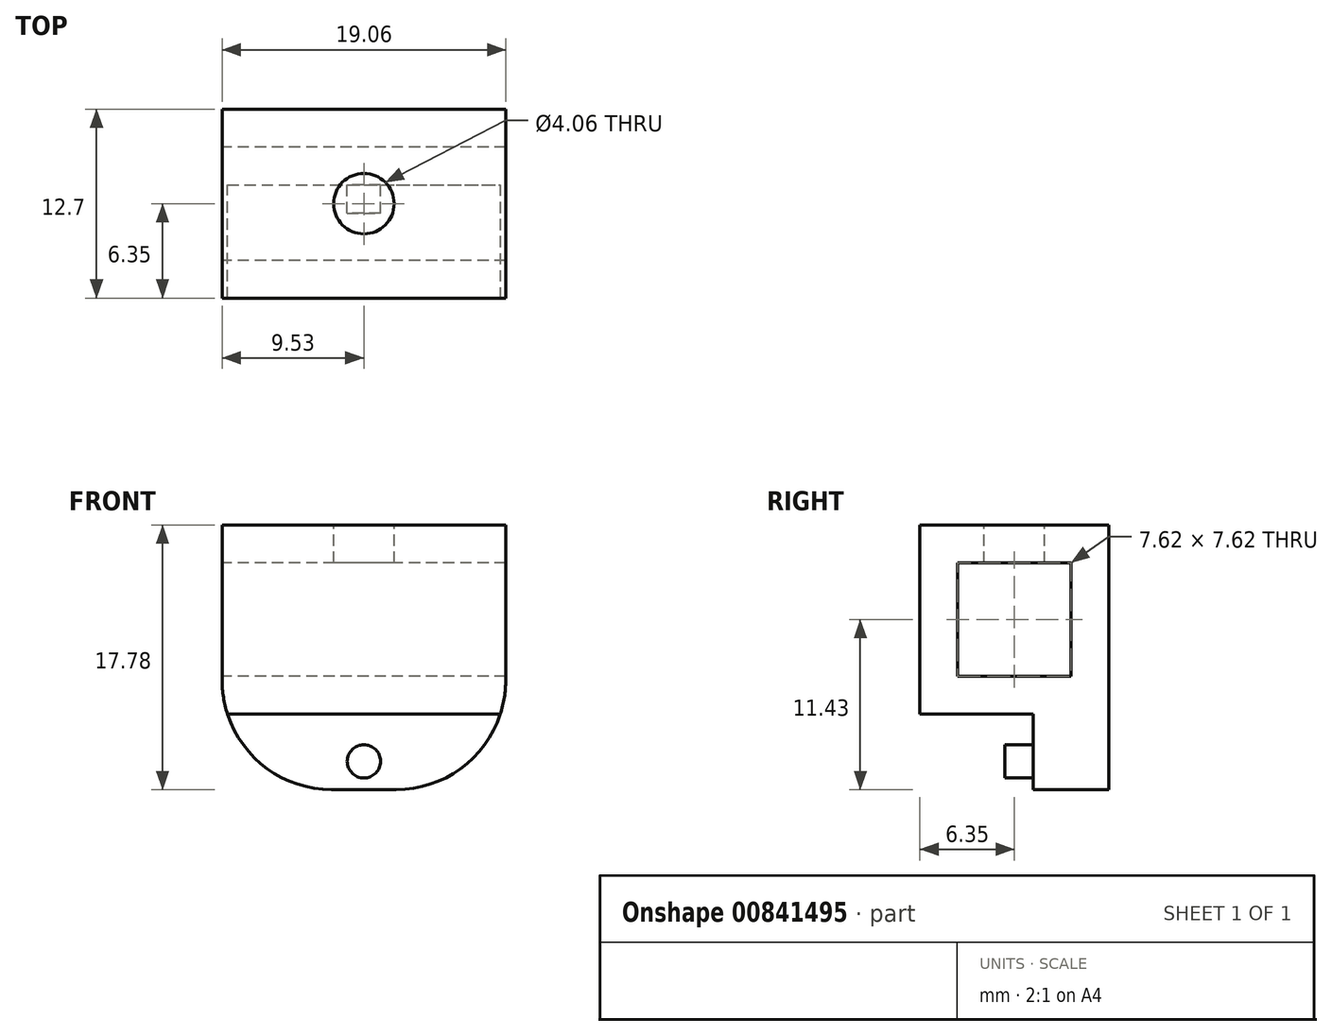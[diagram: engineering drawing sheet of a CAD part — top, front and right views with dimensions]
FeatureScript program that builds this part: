
annotation { "Feature Type Name" : "Feature", "Feature Type Description" : "" }
export const myFeature = defineFeature(function(context is Context, id is Id, definition is map)
    precondition{}
    {
        {
            var Q0;
            Q0=qCreatedBy(makeId("Front.planeOp"),FACE);
            var sketch = newSketch(context, id + "F0", { "sketchPlane" : qUnion([Q0])});
            skLineSegment(sketch, "E0.bottom", {"start": v(9.53, -6.35) * mm, "end": v(-9.52, -6.35) * mm});
            skLineSegment(sketch, "E0.top", {"start": v(9.52, 6.35) * mm, "end": v(-9.53, 6.35) * mm});
            skLineSegment(sketch, "E0.left", {"start": v(9.53, -6.35) * mm, "end": v(9.52, 6.35) * mm});
            skLineSegment(sketch, "E0.right", {"start": v(-9.52, -6.35) * mm, "end": v(-9.53, 6.35) * mm});
            skPoint(sketch, "E0.middle", {"position": v(0, 0) * mm});
            skSolve(sketch);
        }
        {
            var Q0;
            Q0 = qSketchRegion(id + "F0", true);
            extrude(context, id + "F1", {"entities" : qUnion([Q0]), "endBound" : BoundingType.SYMMETRIC, "depth" : 12.7 * mm, "offsetDistance" : 25.4 * mm});
        }
        {
            var Q0;
            Q0=makeQuery(id+"F1.opExtrude","SWEPT_FACE",FACE,{"disambiguationData":[OSD([sQuery(id+"F0.wireOp",EDGE,"E0.left")])]});
            var Q1;
            Q1=makeQuery(id+"F1.opExtrude","SWEPT_FACE",FACE,{"disambiguationData":[OSD([sQuery(id+"F0.wireOp",EDGE,"E0.right")])]});
            shell(context, id + "F2", {"entities" : qUnion([Q0, Q1]), "thickness" : 2.54 * mm});
        }
        {
            var Q0;
            Q0=makeQuery(id+"F1.opExtrude","SWEPT_FACE",FACE,{"disambiguationData":[OSD([sQuery(id+"F0.wireOp",EDGE,"E0.top")])]});
            var sketch = newSketch(context, id + "F3", { "sketchPlane" : qUnion([Q0])});
            skCircle(sketch, "E1", {"center": v(0, 0) * mm, "radius": 2.03 * mm});
            skSolve(sketch);
        }
        {
            var Q0;
            Q0 = qSketchRegion(id + "F3", true);
            extrude(context, id + "F4", {"entities" : qUnion([Q0]), "operationType" : NewBodyOperationType.REMOVE, "oppositeDirection" : true, "depth" : 2.54 * mm, "offsetDistance" : 25.4 * mm});
        }
        {
            var Q0;
            Q0=makeQuery(id+"F1.opExtrude","SWEPT_FACE",FACE,{"disambiguationData":[OSD([sQuery(id+"F0.wireOp",EDGE,"E0.bottom")])]});
            var sketch = newSketch(context, id + "F5", { "sketchPlane" : qUnion([Q0])});
            skLineSegment(sketch, "E2.bottom", {"start": v(-9.52, -1.27) * mm, "end": v(9.53, -1.27) * mm});
            skLineSegment(sketch, "E2.top", {"start": v(-9.52, -6.35) * mm, "end": v(9.53, -6.35) * mm});
            skLineSegment(sketch, "E2.left", {"start": v(-9.52, -1.27) * mm, "end": v(-9.52, -6.35) * mm});
            skLineSegment(sketch, "E2.right", {"start": v(9.53, -1.27) * mm, "end": v(9.53, -6.35) * mm});
            skSolve(sketch);
        }
        {
            var Q0;
            Q0 = qSketchRegion(id + "F5", true);
            extrude(context, id + "F6", {"entities" : qUnion([Q0]), "operationType" : NewBodyOperationType.ADD, "depth" : 5.08 * mm, "offsetDistance" : 25.4 * mm});
        }
        {
            var Q0;
            Q0=makeQuery(id+"F6.opExtrude","SWEPT_FACE",FACE,{"disambiguationData":[OSD([sQuery(id+"F5.wireOp",EDGE,"E2.bottom")])]});
            var sketch = newSketch(context, id + "F7", { "sketchPlane" : qUnion([Q0])});
            skCircle(sketch, "E3", {"center": v(0, -9.53) * mm, "radius": 1.12 * mm});
            skSolve(sketch);
        }
        {
            var Q0;
            Q0=makeQuery(id+"F7.imprint","IMPRINT",FACE,{"disambiguationData":[TD([[makeQuery(id+"F7.imprint","IMPRINT",EDGE,{"derivedFrom":sQuery(id+"F7.wireOp",EDGE,"E3")}),1.0]])]});
            extrude(context, id + "F8", {"entities" : qUnion([Q0]), "operationType" : NewBodyOperationType.ADD, "depth" : 1.9 * mm, "offsetDistance" : 25.4 * mm});
        }
        {
            var Q0;
            Q0=makeQuery(id+"F6.opExtrude","CAP_EDGE",EDGE,{"disambiguationData":[OSD([sQuery(id+"F5.wireOp",EDGE,"E2.right")])],"isStart":false});
            var Q1;
            Q1=makeQuery(id+"F6.opExtrude","CAP_EDGE",EDGE,{"disambiguationData":[OSD([sQuery(id+"F5.wireOp",EDGE,"E2.left")])],"isStart":false});
            fillet(context, id + "F9", {"entities" : qUnion([Q0, Q1]), "radius" : 7.36 * mm, "tangentPropagation" : true, "allowEdgeOverflow" : false});
        }
    });
